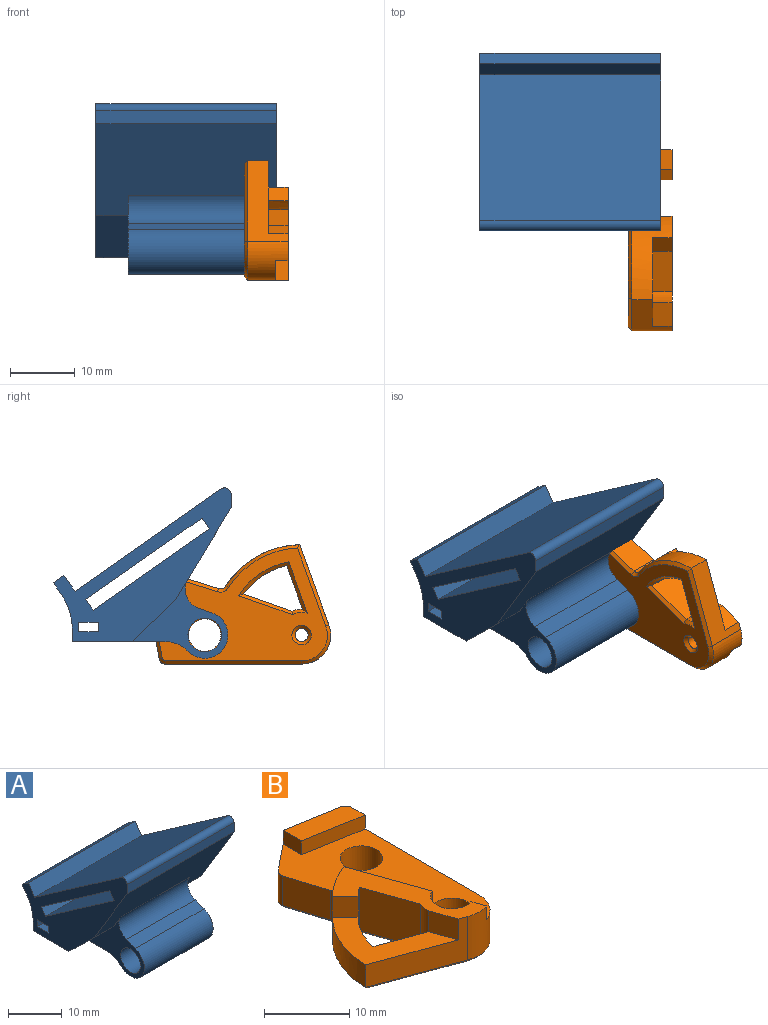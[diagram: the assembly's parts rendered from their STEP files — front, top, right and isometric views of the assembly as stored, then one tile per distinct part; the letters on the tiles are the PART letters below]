
ASSEMBLY  parts=2 mates=1
PART A: 29 faces, bbox 28x27.5x26.4 mm
  f0: cylinder r=2.6mm len=18mm, axis (-1,0,0), area 294.1mm2, adj f23,f25
  f1: cylinder r=5mm len=18mm, axis (-1,0,0), area 71.9mm2, adj f4,f5,f23,f25
  f2: plane 27.52x23.79mm, normal (-1,0,0), area 216.7mm2, adj f5,f7,f8,f9,f10,f11,f12,f13
  f3: plane 18x2.34mm, normal (0,-0.35,0.94), area 45mm2, adj f4,f23,f25,f26
  f4: cylinder r=3.6mm len=18mm, axis (-1,0,0), area 232.4mm2, adj f1,f3,f23,f25
  f5: plane 28x14.34mm, normal (0,0,-1), area 351.5mm2, adj f1,f2,f6,f14,f22,f23,f24,f25
  f6: plane 27.52x23.79mm, normal (1,0,0), area 216.7mm2, adj f5,f7,f8,f9,f10,f11,f12,f13
  f7: plane 28x3mm, normal (0,0,-1), area 84mm2, adj f2,f6,f8,f19
  f8: plane 28x1.5mm, normal (0,-1,0), area 42mm2, adj f2,f6,f7,f9
  f9: plane 28x3mm, normal (0,0,1), area 84mm2, adj f2,f6,f8,f19
  f10: plane 28x2.46mm, normal (0,-0.82,0.57), area 84mm2, adj f2,f6,f11,f20
  f11: plane 28x22.59mm, normal (0,0.57,0.82), area 772.2mm2, adj f2,f6,f10,f27
  f12: plane 28x2.08mm, normal (0,-1,0), area 58.2mm2, adj f2,f6,f13,f27
  f13: plane 28x14.21mm, normal (0,-0.86,-0.52), area 399.3mm2, adj f2,f6,f12,f22,f23,f24,f25,f26
  f14: plane 28x1.73mm, normal (0,1,0), area 48.5mm2, adj f2,f5,f6,f28
  f15: plane 28x1.63mm, normal (0,0.82,-0.57), area 55.7mm2, adj f2,f6,f20,f28
  f16: plane 28x18.02mm, normal (0,-0.57,-0.82), area 616mm2, adj f2,f6,f17,f21
  f17: plane 28x1.64mm, normal (0,-0.82,0.57), area 56mm2, adj f2,f6,f16,f18
  f18: plane 28x18.02mm, normal (0,0.57,0.82), area 616mm2, adj f2,f6,f17,f21
  f19: plane 28x1.5mm, normal (0,1,0), area 42mm2, adj f2,f6,f7,f9
  f20: plane 28x1.64mm, normal (0,0.57,0.82), area 56mm2, adj f2,f6,f10,f15
  f21: plane 28x1.64mm, normal (0,0.82,-0.57), area 56mm2, adj f2,f6,f16,f18
  f22: plane 6.66x6.5mm, normal (0,-0.7,-0.72), area 46.5mm2, adj f5,f6,f13,f23
  f23: plane 14.76x12.21mm, normal (1,0,0), area 56.9mm2, adj f0,f1,f3,f4,f5,f13,f22,f26
  f24: plane 6.66x6.5mm, normal (0,-0.7,-0.72), area 46.5mm2, adj f2,f5,f13,f25
  f25: plane 14.76x12.21mm, normal (-1,0,0), area 56.9mm2, adj f0,f1,f3,f4,f5,f13,f24,f26
  f26: cylinder r=3mm len=18mm, axis (-1,0,0), area 95mm2, adj f3,f13,f23,f25
  f27: cylinder r=1mm len=28mm, axis (1,0,0), area 61.1mm2, adj f2,f6,f11,f12
  f28: cylinder r=10mm len=28mm, axis (1,0,0), area 171mm2, adj f2,f6,f14,f15
PART B: 45 faces, bbox 18.5x28x6.8 mm
  f0: plane 17.7x11.4mm, normal (0,0,1), area 56mm2, adj f1,f2,f10,f11,f13,f16,f17,f24
  f1: plane 12.46x6.25mm, normal (-0.34,-0.94,0), area 46.8mm2, adj f0,f10,f11,f26,f28,f35
  f2: cylinder r=11mm len=6.66mm, axis (0,0,1), area 32.1mm2, adj f0,f3,f25,f27,f28,f29
  f3: plane 6.76x3.25mm, normal (0.34,0.94,0), area 23.4mm2, adj f2,f24,f28,f31
  f4: plane 26.98x17.48mm, normal (0,0,-1), area 255mm2, adj f29,f30,f31,f32,f33,f34,f35,f36
  f5: plane 27.75x13.64mm, normal (0,0,1), area 166.5mm2, adj f6,f8,f9,f10,f11,f12,f13,f16
  f6: plane 21.08x6.25mm, normal (1,0,0), area 94mm2, adj f5,f11,f19,f20,f22,f39
  f7: plane 8.17x6.25mm, normal (0.17,0.98,0), area 51.9mm2, adj f8,f18,f20,f22,f42
  f8: plane 4.27x4.25mm, normal (-0.63,0.78,0), area 23.3mm2, adj f5,f7,f23,f40
  f9: plane 6.09x4.25mm, normal (-0.95,-0.3,0), area 27.1mm2, adj f5,f21,f23,f36
  f10: cylinder r=14mm len=12.89mm, axis (0,0,-1), area 59.8mm2, adj f0,f1,f5,f17,f21,f27,f28,f33
  f11: cylinder r=4.5mm len=6.25mm, axis (0,0,-1), area 42.9mm2, adj f0,f1,f5,f6,f16,f37
  f12: cylinder r=2.5mm len=5mm, axis (0,0,-1), area 66.8mm2, adj f5,f44
  f13: cylinder r=2.5mm len=5mm, axis (0,0,-1), area 58.9mm2, adj f0,f5,f15,f16,f17
  f14: cylinder r=1mm len=2mm, axis (0,0,-1), area 9.4mm2, adj f15,f43
  f15: plane 5x5mm, normal (0,0,1), area 16.5mm2, adj f13,f14
  f16: plane 2x1.89mm, normal (0.94,0.33,0), area 4mm2, adj f0,f5,f11,f13
  f17: plane 10.84x3.83mm, normal (0.94,0.33,0), area 23mm2, adj f0,f5,f10,f13
  f18: plane 3.05x2mm, normal (-1,0,0), area 6.1mm2, adj f5,f7,f19,f20
  f19: plane 9x2mm, normal (-0.17,-0.98,0), area 18.3mm2, adj f5,f6,f18,f20
  f20: plane 9x4.63mm, normal (0,0,1), area 27.3mm2, adj f6,f7,f18,f19,f22
  f21: cylinder r=1mm len=4.25mm, axis (0,0,-1), area 5.5mm2, adj f5,f9,f10,f34
  f22: cylinder r=1mm len=6.25mm, axis (0,0,1), area 8.7mm2, adj f6,f7,f20,f41
  f23: cylinder r=1mm len=4.25mm, axis (0,0,1), area 5.1mm2, adj f5,f8,f9,f38
  f24: cylinder r=4mm len=6.25mm, axis (0,0,1), area 10.5mm2, adj f0,f3,f25,f26,f32
  f25: plane 7.48x6.25mm, normal (-0.94,-0.33,0), area 49.6mm2, adj f0,f2,f24,f30
  f26: plane 3.66x3mm, normal (-0.94,-0.33,0), area 11.7mm2, adj f0,f1,f24,f28
  f27: plane 3x2.12mm, normal (-0.71,-0.71,0), area 9mm2, adj f0,f2,f10,f28
  f28: plane 13.71x11.29mm, normal (0,0,1), area 54.4mm2, adj f1,f2,f3,f10,f26,f27
  f29: cone r=11.5mm half-angle=45deg, axis (0,0,-1), area 6.3mm2, adj f2,f4,f30,f31
  f30: plane 8.29x3.2mm, normal (-0.67,-0.24,-0.71), area 5.9mm2, adj f4,f25,f29,f32
  f31: plane 7.95x3.22mm, normal (0.24,0.66,-0.71), area 5.5mm2, adj f3,f4,f29,f32
  f32: cone r=4mm half-angle=45deg, axis (0,0,1), area 1.4mm2, adj f4,f24,f30,f31
  f33: cone r=14mm half-angle=45deg, axis (0,0,1), area 9.4mm2, adj f4,f10,f34,f35
  f34: cone r=1.5mm half-angle=45deg, axis (0,0,-1), area 1.1mm2, adj f4,f21,f33,f36
  f35: plane 12.63x4.89mm, normal (-0.24,-0.66,-0.71), area 9.2mm2, adj f1,f4,f33,f37
  f36: plane 6.24x2.39mm, normal (-0.67,-0.21,-0.71), area 4.5mm2, adj f4,f9,f34,f38
  f37: cone r=4.5mm half-angle=45deg, axis (0,0,1), area 5.8mm2, adj f4,f11,f35,f39
  f38: cone r=0.5mm half-angle=45deg, axis (0,0,1), area 0.6mm2, adj f4,f23,f36,f40
  f39: plane 21.08x0.5mm, normal (0.71,0,-0.71), area 14.9mm2, adj f4,f6,f37,f41
  f40: plane 4.41x3.84mm, normal (-0.44,0.55,-0.71), area 3.8mm2, adj f4,f8,f38,f42
  f41: cone r=0.5mm half-angle=45deg, axis (0,0,1), area 0.7mm2, adj f4,f22,f39,f42
  f42: plane 8.17x1.93mm, normal (0.12,0.7,-0.71), area 5.8mm2, adj f4,f7,f40,f41
  f43: cone r=1.5mm half-angle=45deg, axis (0,0,-1), area 5.6mm2, adj f4,f14
  f44: cone r=3mm half-angle=45deg, axis (0,0,-1), area 12.2mm2, adj f4,f12
PLACE A t=(8.1,-0.09,-1.81)mm
PLACE B rot(axis=(0,1,0),90deg) t=(17.1,-1.8,-6.5)mm
MATE revolute B.f12 <-> A.f0  axis (-1,0,0) through (17.1,-0.09,-1.81)mm
